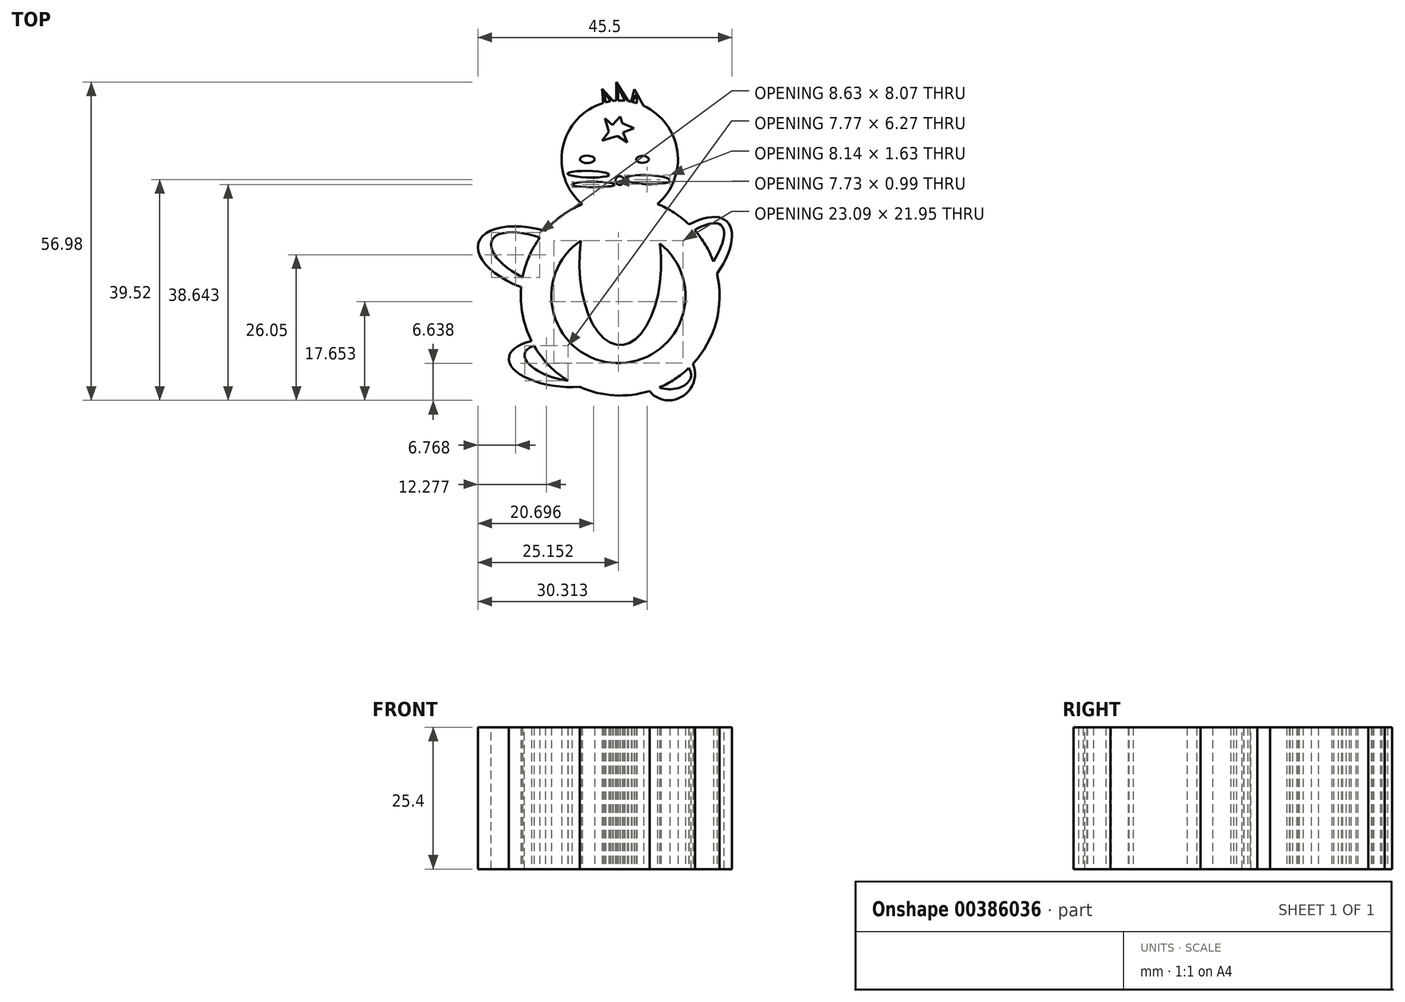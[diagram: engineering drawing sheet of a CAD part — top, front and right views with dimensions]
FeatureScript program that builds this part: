
annotation { "Feature Type Name" : "Feature", "Feature Type Description" : "" }
export const myFeature = defineFeature(function(context is Context, id is Id, definition is map)
    precondition{}
    {
        {
            var Q0;
            Q0=qCreatedBy(makeId("Top.planeOp"),FACE);
            var sketch = newSketch(context, id + "F0", { "sketchPlane" : qUnion([Q0])});
            skArc(sketch, "E0", {"start": v(-35.75, 32.27) * mm, "mid": v(-33.47, 32.54) * mm, "end": v(-31.3, 33.3) * mm});
            skArc(sketch, "E1", {"start": v(-35.84, 2.8) * mm, "mid": v(-20.24, 16.07) * mm, "end": v(-31.3, 33.3) * mm});
            skLineSegment(sketch, "E2", {"start": v(-40.23, 33.21) * mm, "end": v(-40.22, 33.21) * mm});
            skLineSegment(sketch, "E3.MirrorCS", {"start": v(-31.26, 33.18) * mm, "end": v(-31.26, 33.19) * mm});
            skArc(sketch, "E4.MirrorCS", {"start": v(-35.84, 2.8) * mm, "mid": v(-51.35, 16.16) * mm, "end": v(-40.18, 33.32) * mm});
            skPoint(sketch, "E5.trimOffspring.end.orphan", {"position": v(-35.63, 69.5) * mm});
            skPoint(sketch, "E6.start.orphan", {"position": v(-35.86, -3.09) * mm});
            skArc(sketch, "E7.trimOffspring", {"start": v(-35.75, 32.27) * mm, "mid": v(-38.02, 32.55) * mm, "end": v(-40.18, 33.32) * mm});
            skLineSegment(sketch, "E8", {"start": v(-40.18, 33.32) * mm, "end": v(-40.18, 33.32) * mm});
            skPoint(sketch, "E9.0.internal.orphan", {"position": v(-42.32, 42.83) * mm});
            skPoint(sketch, "E9.1.internal.orphan", {"position": v(-40.64, 42.83) * mm});
            skEllipse(sketch, "E10", {"center": v(-41.51, 42.83) * mm, "majorRadius": 1.32 * mm, "minorRadius": 0.66 * mm, "majorAxis": v(1, 0)});
            skEllipse(sketch, "E11", {"center": v(-31.62, 42.83) * mm, "majorRadius": 1.13 * mm, "minorRadius": 0.62 * mm, "majorAxis": v(1, 0)});
            skPoint(sketch, "E12.first.point", {"position": v(-35.7, 39.04) * mm});
            skPoint(sketch, "E12.second.point", {"position": v(-35.62, 37.9) * mm});
            skPoint(sketch, "E12.third.point", {"position": v(-35.12, 38.54) * mm});
            skEllipticalArc(sketch, "E13", {});
            skEllipticalArc(sketch, "E14", {});
            skCircle(sketch, "E15", {"center": v(-35.7, 39.04) * mm, "radius": 0.77 * mm});
            skLineSegment(sketch, "E16", {"start": v(-35.62, 50.52) * mm, "end": v(-37, 49) * mm});
            skLineSegment(sketch, "E17", {"start": v(-37, 49) * mm, "end": v(-38.34, 50.2) * mm});
            skLineSegment(sketch, "E18", {"start": v(-38.34, 50.2) * mm, "end": v(-37.66, 47.76) * mm});
            skLineSegment(sketch, "E19", {"start": v(-37.66, 47.76) * mm, "end": v(-38.9, 46.16) * mm});
            skLineSegment(sketch, "E20", {"start": v(-38.9, 46.16) * mm, "end": v(-36.13, 47.03) * mm});
            skLineSegment(sketch, "E21", {"start": v(-36.13, 47.03) * mm, "end": v(-34.39, 45.87) * mm});
            skLineSegment(sketch, "E22", {"start": v(-34.39, 45.87) * mm, "end": v(-35.12, 47.61) * mm});
            skLineSegment(sketch, "E23", {"start": v(-35.12, 47.61) * mm, "end": v(-33.16, 48.43) * mm});
            skLineSegment(sketch, "E24", {"start": v(-33.16, 48.43) * mm, "end": v(-35.26, 49.29) * mm});
            skLineSegment(sketch, "E25", {"start": v(-35.26, 49.29) * mm, "end": v(-35.62, 50.52) * mm});
            skEllipticalArc(sketch, "E26", {});
            skEllipticalArc(sketch, "E27", {});
            skArc(sketch, "E28", {"start": v(-39.81, 29.72) * mm, "mid": v(-36.33, 6.36) * mm, "end": v(-31.37, 29.45) * mm});
            skArc(sketch, "E29", {"start": v(-42.43, 34.8) * mm, "mid": v(-35.57, 0.56) * mm, "end": v(-28.94, 34.84) * mm});
            skEllipticalArc(sketch, "E30", {});
            skEllipticalArc(sketch, "E31.trimOffspring", {});
            skCircle(sketch, "E32", {"center": v(-35.57, 42.83) * mm, "radius": 10.08 * mm});
            skArc(sketch, "E33.trimOffspring", {"start": v(-28.94, 34.84) * mm, "mid": v(-25.93, 46.43) * mm, "end": v(-35.68, 53.4) * mm});
            skArc(sketch, "E34.trimOffspring", {"start": v(-42.43, 34.8) * mm, "mid": v(-45.5, 46.43) * mm, "end": v(-35.68, 53.4) * mm});
            skEllipticalArc(sketch, "E35", {});
            skEllipse(sketch, "E36", {"center": v(-41.32, 40.17) * mm, "majorRadius": 3.74 * mm, "minorRadius": 0.58 * mm, "majorAxis": v(1, -0.03)});
            skEllipse(sketch, "E37", {"center": v(-40.4, 38.32) * mm, "majorRadius": 3.86 * mm, "minorRadius": 0.5 * mm, "majorAxis": v(1, 0)});
            skEllipse(sketch, "E38", {"center": v(-30.79, 39.2) * mm, "majorRadius": 4.07 * mm, "minorRadius": 0.81 * mm, "majorAxis": v(1, -0.04)});
            skEllipticalArc(sketch, "E39", {});
            skEllipticalArc(sketch, "E40.trimOffspring", {});
            skEllipticalArc(sketch, "E41", {});
            skPoint(sketch, "E42.end.orphan", {"position": v(-33.8, 55.17) * mm});
            skPoint(sketch, "E43.end.orphan", {"position": v(-36.03, 55.17) * mm});
            skPoint(sketch, "E44.start.orphan", {"position": v(-35.63, 55.17) * mm});
            skLineSegment(sketch, "E45", {"start": v(-38.22, 53.05) * mm, "end": v(-38.48, 54.8) * mm});
            skLineSegment(sketch, "E46", {"start": v(-38.48, 54.8) * mm, "end": v(-37.33, 53.24) * mm});
            skLineSegment(sketch, "E47", {"start": v(-36, 53.38) * mm, "end": v(-36.03, 55.87) * mm});
            skLineSegment(sketch, "E48", {"start": v(-32.66, 54.57) * mm, "end": v(-32.66, 52.9) * mm});
            skLineSegment(sketch, "E49.trimOffspring", {"start": v(-33.52, 53.13) * mm, "end": v(-32.66, 54.57) * mm});
            skLineSegment(sketch, "E50", {"start": v(-38.7, 52.92) * mm, "end": v(-38.9, 55.46) * mm});
            skLineSegment(sketch, "E51", {"start": v(-38.9, 55.46) * mm, "end": v(-36.9, 53.3) * mm});
            skLineSegment(sketch, "E52", {"start": v(-36.32, 56.66) * mm, "end": v(-34.18, 53.26) * mm});
            skLineSegment(sketch, "E53", {"start": v(-33.1, 55.36) * mm, "end": v(-31.43, 52.42) * mm});
            skLineSegment(sketch, "E54.trimOffspring", {"start": v(-33.69, 53.17) * mm, "end": v(-33.1, 55.36) * mm});
            skLineSegment(sketch, "E55.trimOffspring", {"start": v(-36.32, 53.36) * mm, "end": v(-36.32, 56.66) * mm});
            skLineSegment(sketch, "E56", {"start": v(-36.03, 55.87) * mm, "end": v(-34.8, 53.34) * mm});
            const initialGuessF0  = {"E13": [-0.050170236395381804, 0.024659696109714902, 0.9191317181264255, -0.3939503582102257, 0.009199655081600335, 0.003936130440226184, 1.734466814911847, 4.545235842981665], "E14": [-0.02479391731321382, 0.02315056510268358, 0.6782801316770759, 0.7348034179099391, 0.01069129768041329, 0.003802890823947562, 5.197525058086832, 0.8776771338511572], "E26": [-0.02674462087452731, 0.004242688883091448, 1, 0, 0.0038295928388834, 0.002553061582148075, 4.209354226281871, 0.49256931975431095], "E27": [-0.04592141702103773, 0.006411571239290696, 0.9714845126181276, -0.23710301926192173, 0.00699388107466369, 0.0029930447534914735, 2.521336834579684, 4.960907051741792], "E30": [-0.050170236395381804, 0.024659696109714902, 0.9580229339275251, -0.28669157306920773, 0.011293539354467783, 0.005497205965667889, 1.6113627075158532, 4.561739043398052], "E31.trimOffspring": [-0.024793917313216743, 0.023150565102696294, 0.6970705879518836, 0.7170025072567148, 0.011910155665079187, 0.005521084002145903, 5.052520364289157, 0.9629552687813783], "E35": [-0.03562771156429667, 0.024199362844228554, 0, -1, 0.014619797468173365, 0.007319114842854429, 4.427452265282606, 1.8187665500918035], "E39": [-0.04592141702103773, 0.006411571239290696, 0.9958187945169195, -0.09135058011238538, 0.009675933529645145, 0.004284223413355197, 2.229662937823154, 5.072161964596333], "E40.trimOffspring": [-0.02674462087452731, 0.004242688883091448, 0.7929066203318414, -0.609343163934689, 0.00443422596166132, 0.004644453599734034, 4.4598623858394095, 1.083393042040382], "E41": [-0.03562771156429667, 0.024199362844228554, 0, -1, 0.010648285970096979, 0.004891043903843526, 4.167768259385751, 2.0860765319716172]};
            skSetInitialGuess(sketch, initialGuessF0);
            skSolve(sketch);
        }
        {
            var Q0;
            Q0 = qSketchRegion(id + "F0", true);
            var Q1;
            Q1=makeQuery(id+"F0.imprint","IMPRINT",FACE,{"disambiguationData":[TD([[makeQuery(id+"F0.imprint","IMPRINT",EDGE,{"derivedFrom":sQuery(id+"F0.wireOp",EDGE,"E0")}),-1.0]])]});
            var Q2;
            {var subQ2=sQuery(id+"F0.wireOp",EDGE,"E35");Q2=makeQuery(id+"F0.imprint","IMPRINT",FACE,{"disambiguationData":[TD([[makeQuery(id+"F0.imprint","IMPRINT",EDGE,{"derivedFrom":subQ2}),1.0]])]});}
            var Q3;
            Q3=makeQuery(id+"F0.imprint","IMPRINT",FACE,{"disambiguationData":[TD([[makeQuery(id+"F0.imprint","IMPRINT",EDGE,{"derivedFrom":sQuery(id+"F0.wireOp",EDGE,"E10")}),-1.0]])]});
            extrude(context, id + "F1", {"entities" : qUnion([Q0, Q1, Q2, Q3]), "depth" : 25.4 * mm});
        }
    });
